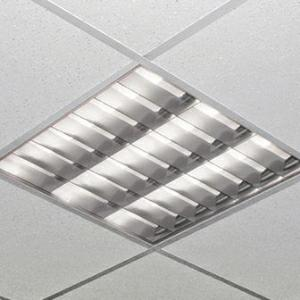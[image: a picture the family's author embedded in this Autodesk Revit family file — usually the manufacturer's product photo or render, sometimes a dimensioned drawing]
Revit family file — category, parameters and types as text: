
# Revit family: 3f_filippi_-_l_320_2s_3f_filippi_-_28829_-_l_323x10w_led_ep_2s_596x596
name_source: partatom
category: Lighting Fixtures
units: mm (PartAtom-declared; Revit-internal decimal feet)

## family parameters
Cut with Voids When Loaded = No
Host = Face
Light Source = No
Part Type = Normal
Room Calculation Point = No
Round Connector Dimension = Use Diameter
Shared = No

## types (1)
- 3F Filippi - L 320 2S (1 x LED, 3997 lm, 35 W, 4000 K)
    Apparent Load = 35 VA
    Approval mark = ENEC
    CIE Flux Codes = 71 98 100 100 100
    Color Rendering = 80
    Color Temperature = 4000 K
    Control Gear = Electronic ballast
    Default Elevation = 1800 mm
    Description = ILLUMINOTECHNICAL
Luminous efficiency 100% (DLOR 100%, ULOR 0%).
Initial luminous flux of the luminaire 3997 lm.
Emergency luminaire luminous flux BLF 11.4%.
Direct symmetric distribution.
Installation Interdistance Transv.D = 1.21 x hu - Long.D = 1.14 x hu.
Average luminance <1000 cd/m² for radial angles >65°.
Tabular UGR (CIE 117 - 4H-8H; S=0.25H; 70/50/20): RUG 14.7 - 15.3.
Beam angle: 87° - 86°.
Luminous efficacy 114 lm/W.
Lifetime (L93/B10): 30000 h. (tq+25°C)
Lifetime (L90/B10): 50000 h. (tq+25°C)
Lifetime (L85/B10): 80000 h. (tq+25°C)
Lifetime (L80/B10): 100000 h. (tq+25°C)
Sudden decreased luminous flux after 50000 hours: 0% (C0).
Photobiological safety in compliance with IEC/TR 62778: RG0 risk exempt, (IEC 62471).
In compliance with IEC/EN 62722-2-1 - IEC/EN 62717 standards.

SOURCE
3 linear LED modules 10W/840.
Energy efficiency class (UE 2019/2020 - UE 2019/2015): D.
CIE 13.3 Colour rendering index: CRI >80 (R9 <50%).
IES TM-30 Fidelity Index: Rf = 84 Rg = 95.
CCT nominal colour temperature 4000 K.
Colour initial tolerance (MacAdam): SDCM 2.

MECHANICAL
Housing in hot-galvanised steel, painted in white polyester.
2S parabolic louvre in semi-specular aluminium, non-reflecting, with transverse blades closed at the top.
Prismatic flat diffusers in transparent methacrylate (PMMA), multilenticular, anti-glare, prismatic outer surface, positioned above the louvre blades.
Film protective against dust and finger marks, adhesive, attached to louvre.
Luminaire with limited surface temperature. - D - (EN 60598-2-24)
Dimensions: 596x596 mm, height 80 mm. Weight 4.75 kg.
IP20 protection degree.
Mechanical strength to impacts IK02 (0.2 joule).
Glow-wire test resistance 650°C.

ELECTRICAL
Halogen Free electronic wiring 230V-50/60Hz, power factor 0.85, THD <25%, constant output current, SELV, class I, 1 driver.
Power of the luminaire 35 W.
CE - IEC 60598-1 - EN 60598-1.
EP maintained emergency wiring on board, 1h duration, 24h recharge; compliant with EN 60598-2-22, excluding high risk areas.
SAFE FLICKER: PstLM=<1 and SVM=<0.4 (IEC TR 61547-1 and IEC TR 63158), to ensure a more comfortable and safe light.
Ambient temperature from +5°C to +25°C.
Temperature class T6 max 85°C.
Relative humidity UR: <85%.

INSTALLATION
Lay-in recessed fitting.
On request: pull-up recessed fitting with brackets.
False ceiling carving: 580x580 mm.
All accessories dedicated to this product are available on the Catalog and on our website www.3F-Filippi.com.

APPLICATIONS
In environments with VDTs, managerial offices and staterooms, public offices and schools.

WARNING
Luminaire designed for disposal/recycling at end-of-life.
Replaceable (LED only) light source by a professional. Replaceable control gear by a professional.
    Height = 0 mm  [stored 0 ft]
    Lamp = 1 x LED
    Lamp Light Flux = 3997 lm
    Lamp Power = 35 W
    Lamp count = 1
    Length = 596 mm
    Lifetime = 50000 h
    Luminous efficacy = 114 lm/W
    Manufacturer = 3F Filippi
    ModVariant = No
    Model = 3F Filippi - 28829 - L 323x10W LED EP 2S 596x596
    Mounting Place = Ceiling
    Mounting Type = Recessed
    Number of Poles = 1
    OnlyDefault = Yes
    Power Factor = 1
    Product Name = 3F Filippi - L 320 2S
    Product group = recessed luminaire
    ProductGroupID = 4
    Protection Class = Protection class I
    Protection Degree = IP 20
    RLX_Detail_Level = 1
    RLX_Emergency_Light_Flux = 0 lm
    RLX_Emergency_Type = 0
    RLX_Emergency_Type_DB = No
    RlxData = <blob elided: 92685 chars, md5=44f90504>
    Socket = socket
    Standby Power = 0 W
    System Light Flux = 3997 lm
    System Power = 35 W
    Type Comments = Product without accessories
    Type Image = 3ffilippi_28829.jpg
    URL = http://relux.com
    VarID = ---
    Voltage = 0 V
    Weight = 0.00 kg
    Width = 596 mm

note: [stored X ft] marks values corroborated as IEEE doubles in the binary element streams (Revit-internal decimal feet)

## geometry (parser evidence)
native form markers: Blend x4, Sweep x10
no freeform markers — native parametric forms only
